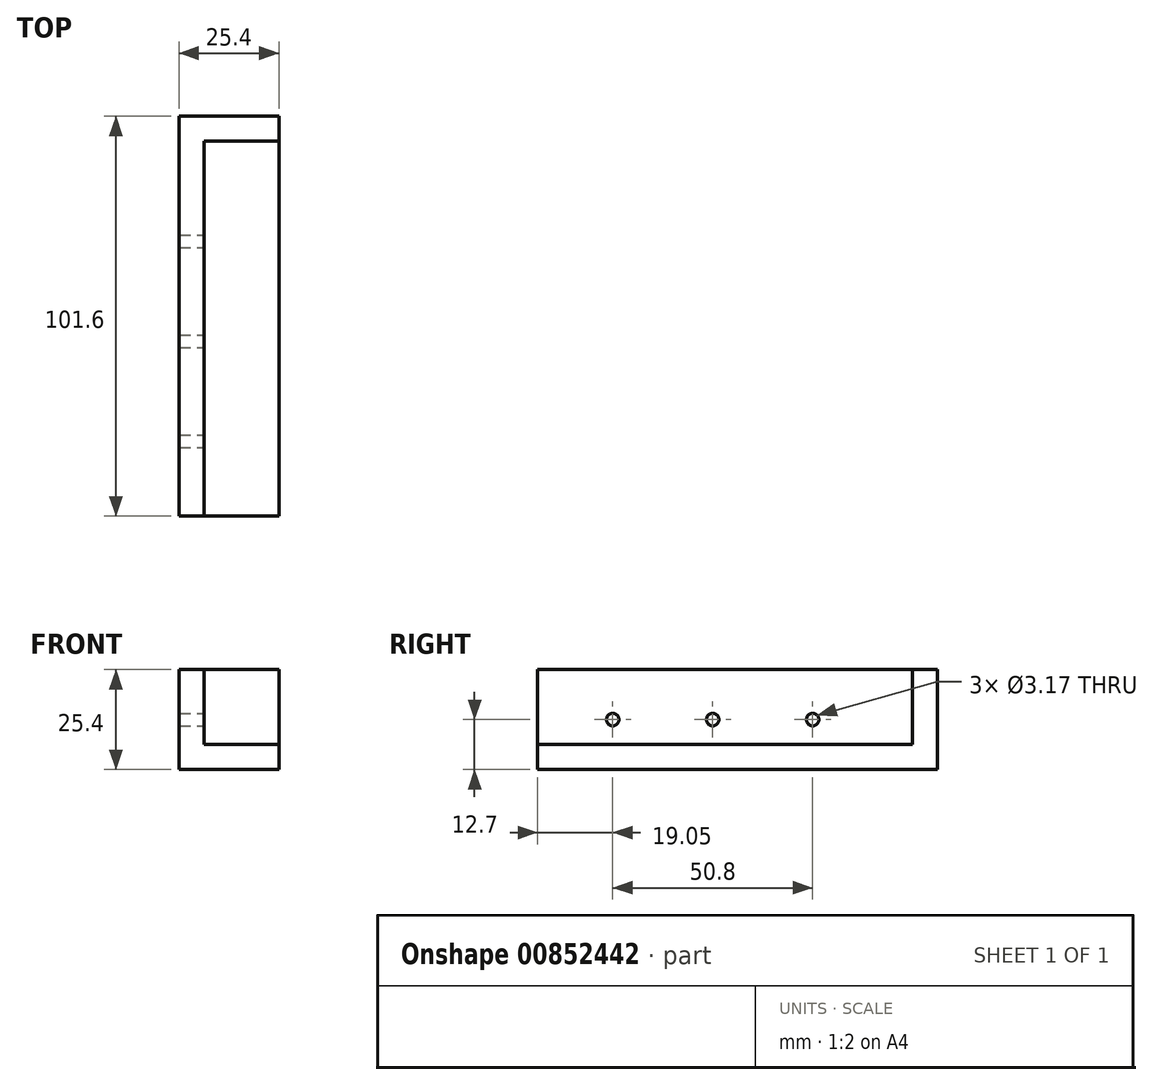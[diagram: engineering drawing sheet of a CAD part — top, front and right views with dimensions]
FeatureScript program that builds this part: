
annotation { "Feature Type Name" : "Feature", "Feature Type Description" : "" }
export const myFeature = defineFeature(function(context is Context, id is Id, definition is map)
    precondition{}
    {
        {
            var Q0;
            Q0=qCreatedBy(makeId("Front.planeOp"),FACE);
            var sketch = newSketch(context, id + "F0", { "sketchPlane" : qUnion([Q0])});
            skLineSegment(sketch, "E0", {"start": v(0, 0) * mm, "end": v(0, 25.4) * mm});
            skLineSegment(sketch, "E1", {"start": v(0, 25.4) * mm, "end": v(6.35, 25.4) * mm});
            skLineSegment(sketch, "E2", {"start": v(6.35, 25.4) * mm, "end": v(6.35, 6.35) * mm});
            skLineSegment(sketch, "E3", {"start": v(6.35, 6.35) * mm, "end": v(25.4, 6.35) * mm});
            skLineSegment(sketch, "E4", {"start": v(25.4, 6.35) * mm, "end": v(25.4, 0) * mm});
            skLineSegment(sketch, "E5", {"start": v(25.4, 0) * mm, "end": v(0, 0) * mm});
            skSolve(sketch);
        }
        {
            var Q0;
            Q0 = qSketchRegion(id + "F0", true);
            extrude(context, id + "F1", {"entities" : qUnion([Q0]), "depth" : 101.6 * mm, "offsetDistance" : 25.4 * mm});
        }
        {
            var Q0;
            Q0=qCreatedBy(makeId("Front.planeOp"),FACE);
            var sketch = newSketch(context, id + "F2", { "sketchPlane" : qUnion([Q0])});
            skLineSegment(sketch, "E6.bottom", {"start": v(0, 0) * mm, "end": v(25.4, 0) * mm});
            skLineSegment(sketch, "E6.top", {"start": v(0, 25.4) * mm, "end": v(25.4, 25.4) * mm});
            skLineSegment(sketch, "E6.left", {"start": v(0, 0) * mm, "end": v(0, 25.4) * mm});
            skLineSegment(sketch, "E6.right", {"start": v(25.4, 0) * mm, "end": v(25.4, 25.4) * mm});
            skSolve(sketch);
        }
        {
            var Q0;
            Q0 = qSketchRegion(id + "F2", true);
            extrude(context, id + "F3", {"entities" : qUnion([Q0]), "operationType" : NewBodyOperationType.ADD, "depth" : 6.35 * mm, "offsetDistance" : 25.4 * mm});
        }
        {
            var Q0;
            Q0=makeQuery(id+"F1.opExtrude","SWEPT_FACE",FACE,{"disambiguationData":[OSD([sQuery(id+"F0.wireOp",EDGE,"E2")])]});
            var sketch = newSketch(context, id + "F4", { "sketchPlane" : qUnion([Q0])});
            skLineSegment(sketch, "E7", {"start": v(-6.35, 12.7) * mm, "end": v(-101.6, 12.7) * mm, "construction": true});
            skCircle(sketch, "E8", {"center": v(-31.75, 12.7) * mm, "radius": 1.59 * mm});
            skCircle(sketch, "E9", {"center": v(-57.15, 12.7) * mm, "radius": 1.59 * mm});
            skCircle(sketch, "E10", {"center": v(-82.55, 12.7) * mm, "radius": 1.59 * mm});
            skSolve(sketch);
        }
        {
            var Q0;
            Q0 = qSketchRegion(id + "F4", true);
            extrude(context, id + "F5", {"entities" : qUnion([Q0]), "operationType" : NewBodyOperationType.REMOVE, "oppositeDirection" : true, "depth" : 25.4 * mm, "offsetDistance" : 25.4 * mm});
        }
    });
